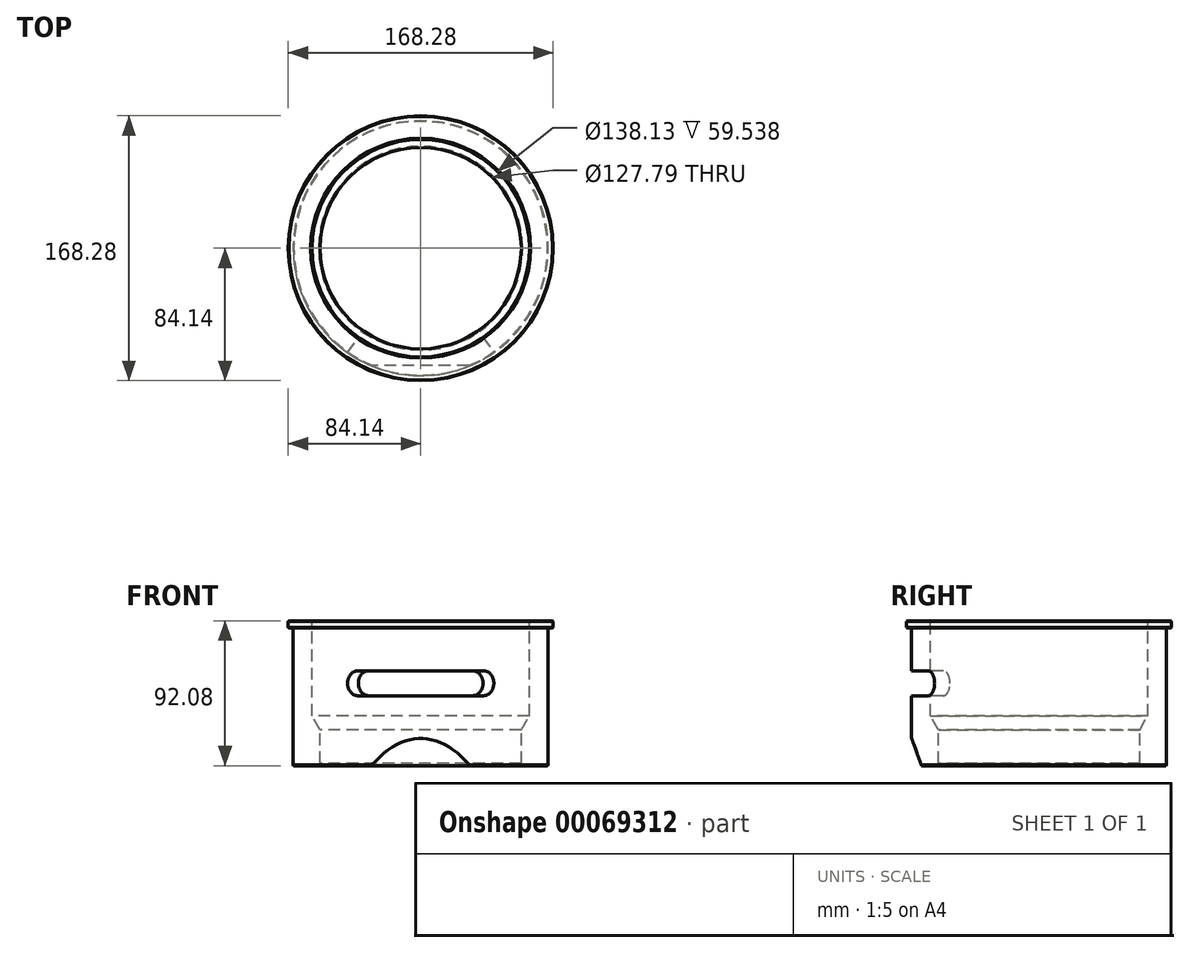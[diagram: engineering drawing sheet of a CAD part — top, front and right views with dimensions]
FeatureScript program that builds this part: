
annotation { "Feature Type Name" : "Feature", "Feature Type Description" : "" }
export const myFeature = defineFeature(function(context is Context, id is Id, definition is map)
    precondition{}
    {
        {
            var Q0;
            Q0=qCreatedBy(makeId("Right.planeOp"),FACE);
            var sketch = newSketch(context, id + "F0", { "sketchPlane" : qUnion([Q0])});
            skLineSegment(sketch, "E0", {"start": v(0, 0) * mm, "end": v(0, -92.08) * mm, "construction": true});
            skLineSegment(sketch, "E1.0", {"start": v(84.14, 0) * mm, "end": v(84.14, -4.52) * mm});
            skLineSegment(sketch, "E2.0", {"start": v(69.06, 0) * mm, "end": v(69.06, -60.33) * mm});
            skLineSegment(sketch, "E3", {"start": v(84.14, 0) * mm, "end": v(69.06, 0) * mm});
            skLineSegment(sketch, "E4.0", {"start": v(80.96, -4.52) * mm, "end": v(80.96, -92.08) * mm});
            skLineSegment(sketch, "E5", {"start": v(84.14, -4.52) * mm, "end": v(80.96, -4.52) * mm});
            skLineSegment(sketch, "E6.0", {"start": v(63.9, -69.28) * mm, "end": v(63.9, -92.08) * mm});
            skLineSegment(sketch, "E7", {"start": v(69.06, -60.33) * mm, "end": v(63.9, -69.28) * mm});
            skLineSegment(sketch, "E8", {"start": v(63.9, -92.08) * mm, "end": v(80.96, -92.08) * mm});
            skSolve(sketch);
        }
        {
            var Q0;
            Q0=makeQuery(id+"F0.imprint","IMPRINT",FACE,{"disambiguationData":[TD([[makeQuery(id+"F0.imprint","IMPRINT",EDGE,{"derivedFrom":sQuery(id+"F0.wireOp",EDGE,"E1.0")}),-1.0]])]});
            var Q1;
            Q1=sQuery(id+"F0.wireOp",EDGE,"E0");
            revolve(context, id + "F1", {"entities" : qUnion([Q0]), "axis" : qUnion([Q1]), "revolveType" : RevolveType.FULL});
        }
        {
            var Q0;
            Q0=makeQuery(id+"F1.opRevolve","SWEPT_EDGE",EDGE,{"disambiguationData":[OSD([sQuery(id+"F0.wireOp",EDGE,"E4.0"),sQuery(id+"F0.wireOp",EDGE,"E5")])]});
            fillet(context, id + "F2", {"entities" : qUnion([Q0]), "radius" : 0.38 * mm, "tangentPropagation" : true, "allowEdgeOverflow" : false});
        }
        {
            var Q0;
            Q0=makeQuery(id+"F1.opRevolve","SWEPT_FACE",FACE,{"disambiguationData":[OSD([sQuery(id+"F0.wireOp",EDGE,"E1.0")])]});
            chamfer(context, id + "F3", {"entities" : qUnion([Q0]), "width" : 0.38 * mm, "tangentPropagation" : true});
        }
        {
            var Q0;
            Q0=makeQuery(id+"F1.opRevolve","SWEPT_EDGE",EDGE,{"disambiguationData":[OSD([sQuery(id+"F0.wireOp",EDGE,"E2.0"),sQuery(id+"F0.wireOp",EDGE,"E3")])]});
            chamfer(context, id + "F4", {"entities" : qUnion([Q0]), "width" : 0.79 * mm, "tangentPropagation" : true});
        }
        {
            var Q0;
            Q0=makeQuery(id+"F1.opRevolve","SWEPT_EDGE",EDGE,{"disambiguationData":[OSD([sQuery(id+"F0.wireOp",EDGE,"E6.0"),sQuery(id+"F0.wireOp",EDGE,"E8")])]});
            chamfer(context, id + "F5", {"entities" : qUnion([Q0]), "chamferType" : ChamferType.OFFSET_ANGLE, "width" : 1.57 * mm, "oppositeDirection" : true, "angle" : 30 * degree, "tangentPropagation" : true});
        }
        {
            var Q0;
            Q0=qCreatedBy(makeId("Right.planeOp"),FACE);
            var sketch = newSketch(context, id + "F6", { "sketchPlane" : qUnion([Q0])});
            skPoint(sketch, "E9", {"position": v(-80.96, -92.08) * mm});
            skLineSegment(sketch, "E10", {"start": v(-80.96, -92.08) * mm, "end": v(-74.61, -92.08) * mm});
            skLineSegment(sketch, "E11", {"start": v(-80.96, -92.08) * mm, "end": v(-80.96, -74.63) * mm});
            skLineSegment(sketch, "E12", {"start": v(-74.61, -92.08) * mm, "end": v(-80.96, -74.63) * mm});
            skSolve(sketch);
        }
        {
            var Q0;
            Q0 = qSketchRegion(id + "F6", true);
            extrude(context, id + "F7", {"entities" : qUnion([Q0]), "operationType" : NewBodyOperationType.REMOVE, "endBound" : BoundingType.THROUGH_ALL, "depth" : 25.4 * mm, "hasSecondDirection" : true, "secondDirectionBound" : SecondDirectionBoundingType.THROUGH_ALL, "secondDirectionOppositeDirection" : true, "secondDirectionDepth" : 25.4 * mm});
        }
        {
            var Q0;
            Q0=makeQuery(id+"F1.opRevolve","SWEPT_EDGE",EDGE,{"disambiguationData":[OSD([sQuery(id+"F0.wireOp",EDGE,"E4.0"),sQuery(id+"F0.wireOp",EDGE,"E8")])]});
            chamfer(context, id + "F8", {"entities" : qUnion([Q0]), "width" : 0.38 * mm, "tangentPropagation" : true});
        }
        {
            var Q0;
            Q0=makeQuery(id+"F1.opRevolve","SWEPT_FACE",FACE,{"disambiguationData":[OSD([sQuery(id+"F0.wireOp",EDGE,"E3")])]});
            cPlane(context, id + "F9", {"entities" : qUnion([Q0]), "cplaneType" : CPlaneType.OFFSET, "offset" : 31.75 * mm, "oppositeDirection" : true, "width" : 152.4 * mm, "height" : 152.4 * mm});
        }
        {
            var Q0;
            Q0=qCreatedBy(id+"F9.planeOp",FACE);
            var sketch = newSketch(context, id + "F10", { "sketchPlane" : qUnion([Q0])});
            skArc(sketch, "E13", {"start": v(-46.44, -66.32) * mm, "mid": v(0, -80.96) * mm, "end": v(46.44, -66.32) * mm});
            skArc(sketch, "E14", {"start": v(-39.61, -56.57) * mm, "mid": v(0, -69.06) * mm, "end": v(39.61, -56.57) * mm});
            skLineSegment(sketch, "E15", {"start": v(-39.61, -56.57) * mm, "end": v(-46.44, -66.32) * mm});
            skLineSegment(sketch, "E16.MirrorCS", {"start": v(39.61, -56.57) * mm, "end": v(46.44, -66.32) * mm});
            skSolve(sketch);
        }
        {
            var Q0;
            Q0 = qSketchRegion(id + "F10", true);
            extrude(context, id + "F11", {"entities" : qUnion([Q0]), "operationType" : NewBodyOperationType.REMOVE, "oppositeDirection" : true, "depth" : 15.88 * mm});
        }
        {
            var Q0;
            Q0=makeQuery(id+"F11.boolean.opBoolean","COPY",EDGE,{"derivedFrom":makeQuery(id+"F11.opExtrude","CAP_EDGE",EDGE,{"disambiguationData":[OSD([sQuery(id+"F10.wireOp",EDGE,"E15")])],"isStart":true})});
            var Q1;
            Q1=makeQuery(id+"F11.boolean.opBoolean","COPY",EDGE,{"derivedFrom":makeQuery(id+"F11.opExtrude","CAP_EDGE",EDGE,{"disambiguationData":[OSD([sQuery(id+"F10.wireOp",EDGE,"E16.MirrorCS")])],"isStart":true})});
            fillet(context, id + "F12", {"entities" : qUnion([Q0, Q1]), "radius" : 7.94 * mm, "tangentPropagation" : true, "allowEdgeOverflow" : false});
        }
        {
            var Q0;
            Q0=makeQuery(id+"F11.boolean.opBoolean","COPY",EDGE,{"derivedFrom":makeQuery(id+"F11.opExtrude","CAP_EDGE",EDGE,{"disambiguationData":[OSD([sQuery(id+"F10.wireOp",EDGE,"E15")])],"isStart":false})});
            var Q1;
            Q1=makeQuery(id+"F11.boolean.opBoolean","COPY",EDGE,{"derivedFrom":makeQuery(id+"F11.opExtrude","CAP_EDGE",EDGE,{"disambiguationData":[OSD([sQuery(id+"F10.wireOp",EDGE,"E16.MirrorCS")])],"isStart":false})});
            fillet(context, id + "F13", {"entities" : qUnion([Q0, Q1]), "radius" : 7.94 * mm, "tangentPropagation" : true, "allowEdgeOverflow" : false});
        }
    });
